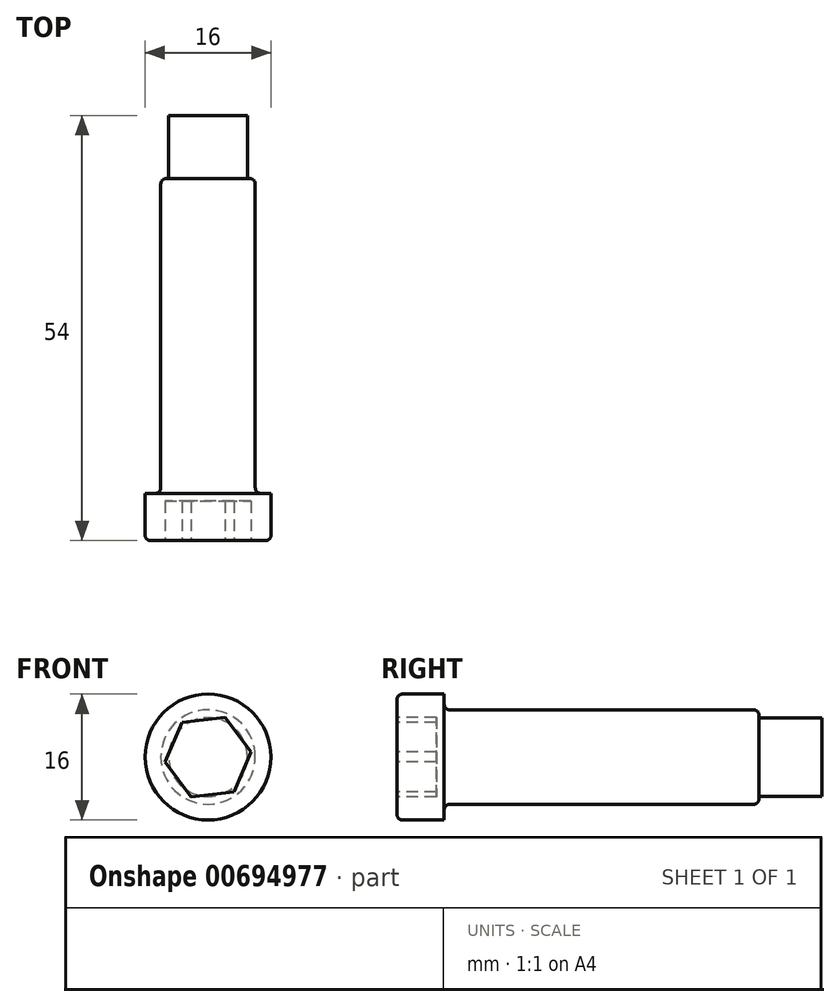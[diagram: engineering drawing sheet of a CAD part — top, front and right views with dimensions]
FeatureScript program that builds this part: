
annotation { "Feature Type Name" : "Feature", "Feature Type Description" : "" }
export const myFeature = defineFeature(function(context is Context, id is Id, definition is map)
    precondition{}
    {
        {
            var Q0;
            Q0=qCreatedBy(makeId("Front.planeOp"),FACE);
            var sketch = newSketch(context, id + "F0", { "sketchPlane" : qUnion([Q0])});
            skCircle(sketch, "E0", {"center": v(0, 0) * mm, "radius": 5 * mm});
            skSolve(sketch);
        }
        {
            var Q0;
            Q0=makeQuery(id+"F0.imprint","IMPRINT",FACE,{"disambiguationData":[TD([[makeQuery(id+"F0.imprint","IMPRINT",EDGE,{"derivedFrom":sQuery(id+"F0.wireOp",EDGE,"E0")}),1.0]])]});
            extrude(context, id + "F1", {"entities" : qUnion([Q0]), "depth" : 8 * mm, "offsetDistance" : 25 * mm});
        }
        {
            var Q0;
            Q0=makeQuery(id+"F1.opExtrude","CAP_FACE",FACE,{"disambiguationData":[OSD([sQuery(id+"F0.wireOp",EDGE,"E0")])],"isStart":false});
            var sketch = newSketch(context, id + "F2", { "sketchPlane" : qUnion([Q0])});
            skCircle(sketch, "E1", {"center": v(0, 0) * mm, "radius": 6 * mm});
            skSolve(sketch);
        }
        {
            var Q0;
            Q0=makeQuery(id+"F2.imprint","IMPRINT",FACE,{"disambiguationData":[TD([[makeQuery(id+"F2.imprint","IMPRINT",EDGE,{"derivedFrom":makeQuery(id+"F1.opExtrude","CAP_EDGE",EDGE,{"disambiguationData":[OSD([sQuery(id+"F0.wireOp",EDGE,"E0")])],"isStart":false})}),1.0]])]});
            var Q1;
            Q1=makeQuery(id+"F2.imprint","IMPRINT",FACE,{"disambiguationData":[TD([[makeQuery(id+"F2.imprint","IMPRINT",EDGE,{"derivedFrom":sQuery(id+"F2.wireOp",EDGE,"E1")}),1.0]])]});
            extrude(context, id + "F3", {"entities" : qUnion([Q0, Q1]), "operationType" : NewBodyOperationType.ADD, "depth" : 40 * mm, "offsetDistance" : 25 * mm});
        }
        {
            var Q0;
            Q0=makeQuery(id+"F3.opExtrude","CAP_FACE",FACE,{"disambiguationData":[OSD([sQuery(id+"F2.wireOp",EDGE,"E1")])],"isStart":false});
            var sketch = newSketch(context, id + "F4", { "sketchPlane" : qUnion([Q0])});
            skCircle(sketch, "E2", {"center": v(0, 0) * mm, "radius": 8 * mm});
            skSolve(sketch);
        }
        {
            var Q0;
            Q0=makeQuery(id+"F4.imprint","IMPRINT",FACE,{"disambiguationData":[TD([[makeQuery(id+"F4.imprint","IMPRINT",EDGE,{"derivedFrom":sQuery(id+"F4.wireOp",EDGE,"E2")}),1.0]])]});
            var Q1;
            Q1=makeQuery(id+"F4.imprint","IMPRINT",FACE,{"disambiguationData":[TD([[makeQuery(id+"F4.imprint","IMPRINT",EDGE,{"derivedFrom":makeQuery(id+"F3.opExtrude","CAP_EDGE",EDGE,{"disambiguationData":[OSD([sQuery(id+"F2.wireOp",EDGE,"E1")])],"isStart":false})}),1.0]])]});
            extrude(context, id + "F5", {"entities" : qUnion([Q0, Q1]), "operationType" : NewBodyOperationType.ADD, "depth" : 6 * mm, "offsetDistance" : 25 * mm});
        }
        {
            var Q0;
            Q0=makeQuery(id+"F5.opExtrude","CAP_FACE",FACE,{"disambiguationData":[OSD([sQuery(id+"F4.wireOp",EDGE,"E2")])],"isStart":false});
            var sketch = newSketch(context, id + "F6", { "sketchPlane" : qUnion([Q0])});
            skCircle(sketch, "E3.cCircle", {"center": v(0, 0) * mm, "radius": 4.77 * mm, "construction": true});
            skLineSegment(sketch, "E3.0", {"start": v(5.47, 0.64) * mm, "end": v(3.29, -4.41) * mm});
            skLineSegment(sketch, "E3.1", {"start": v(3.29, -4.41) * mm, "end": v(-2.18, -5.05) * mm});
            skLineSegment(sketch, "E3.2", {"start": v(-2.18, -5.05) * mm, "end": v(-5.47, -0.64) * mm});
            skLineSegment(sketch, "E3.3", {"start": v(-5.47, -0.64) * mm, "end": v(-3.29, 4.41) * mm});
            skLineSegment(sketch, "E3.4", {"start": v(-3.29, 4.41) * mm, "end": v(2.18, 5.05) * mm});
            skLineSegment(sketch, "E3.5", {"start": v(2.18, 5.05) * mm, "end": v(5.47, 0.64) * mm});
            skPoint(sketch, "E3.0.midPoint", {"position": v(4.38, -1.89) * mm});
            skSolve(sketch);
        }
        {
            var Q0;
            Q0=makeQuery(id+"F6.imprint","IMPRINT",FACE,{"disambiguationData":[TD([[makeQuery(id+"F6.imprint","IMPRINT",EDGE,{"derivedFrom":sQuery(id+"F6.wireOp",EDGE,"E3.0")}),-1.0]])]});
            extrude(context, id + "F7", {"entities" : qUnion([Q0]), "operationType" : NewBodyOperationType.REMOVE, "oppositeDirection" : true, "depth" : 5 * mm, "offsetDistance" : 25 * mm});
        }
        {
            var Q0;
            Q0=makeQuery(id+"F3.opExtrude","SWEPT_FACE",FACE,{"disambiguationData":[OSD([sQuery(id+"F2.wireOp",EDGE,"E1")])]});
            var Q1;
            Q1=makeQuery(id+"F5.opExtrude","CAP_EDGE",EDGE,{"disambiguationData":[OSD([sQuery(id+"F4.wireOp",EDGE,"E2")])],"isStart":false});
            fillet(context, id + "F8", {"entities" : qUnion([Q0, Q1]), "radius" : .7 * mm, "tangentPropagation" : true, "allowEdgeOverflow" : false});
        }
    });
